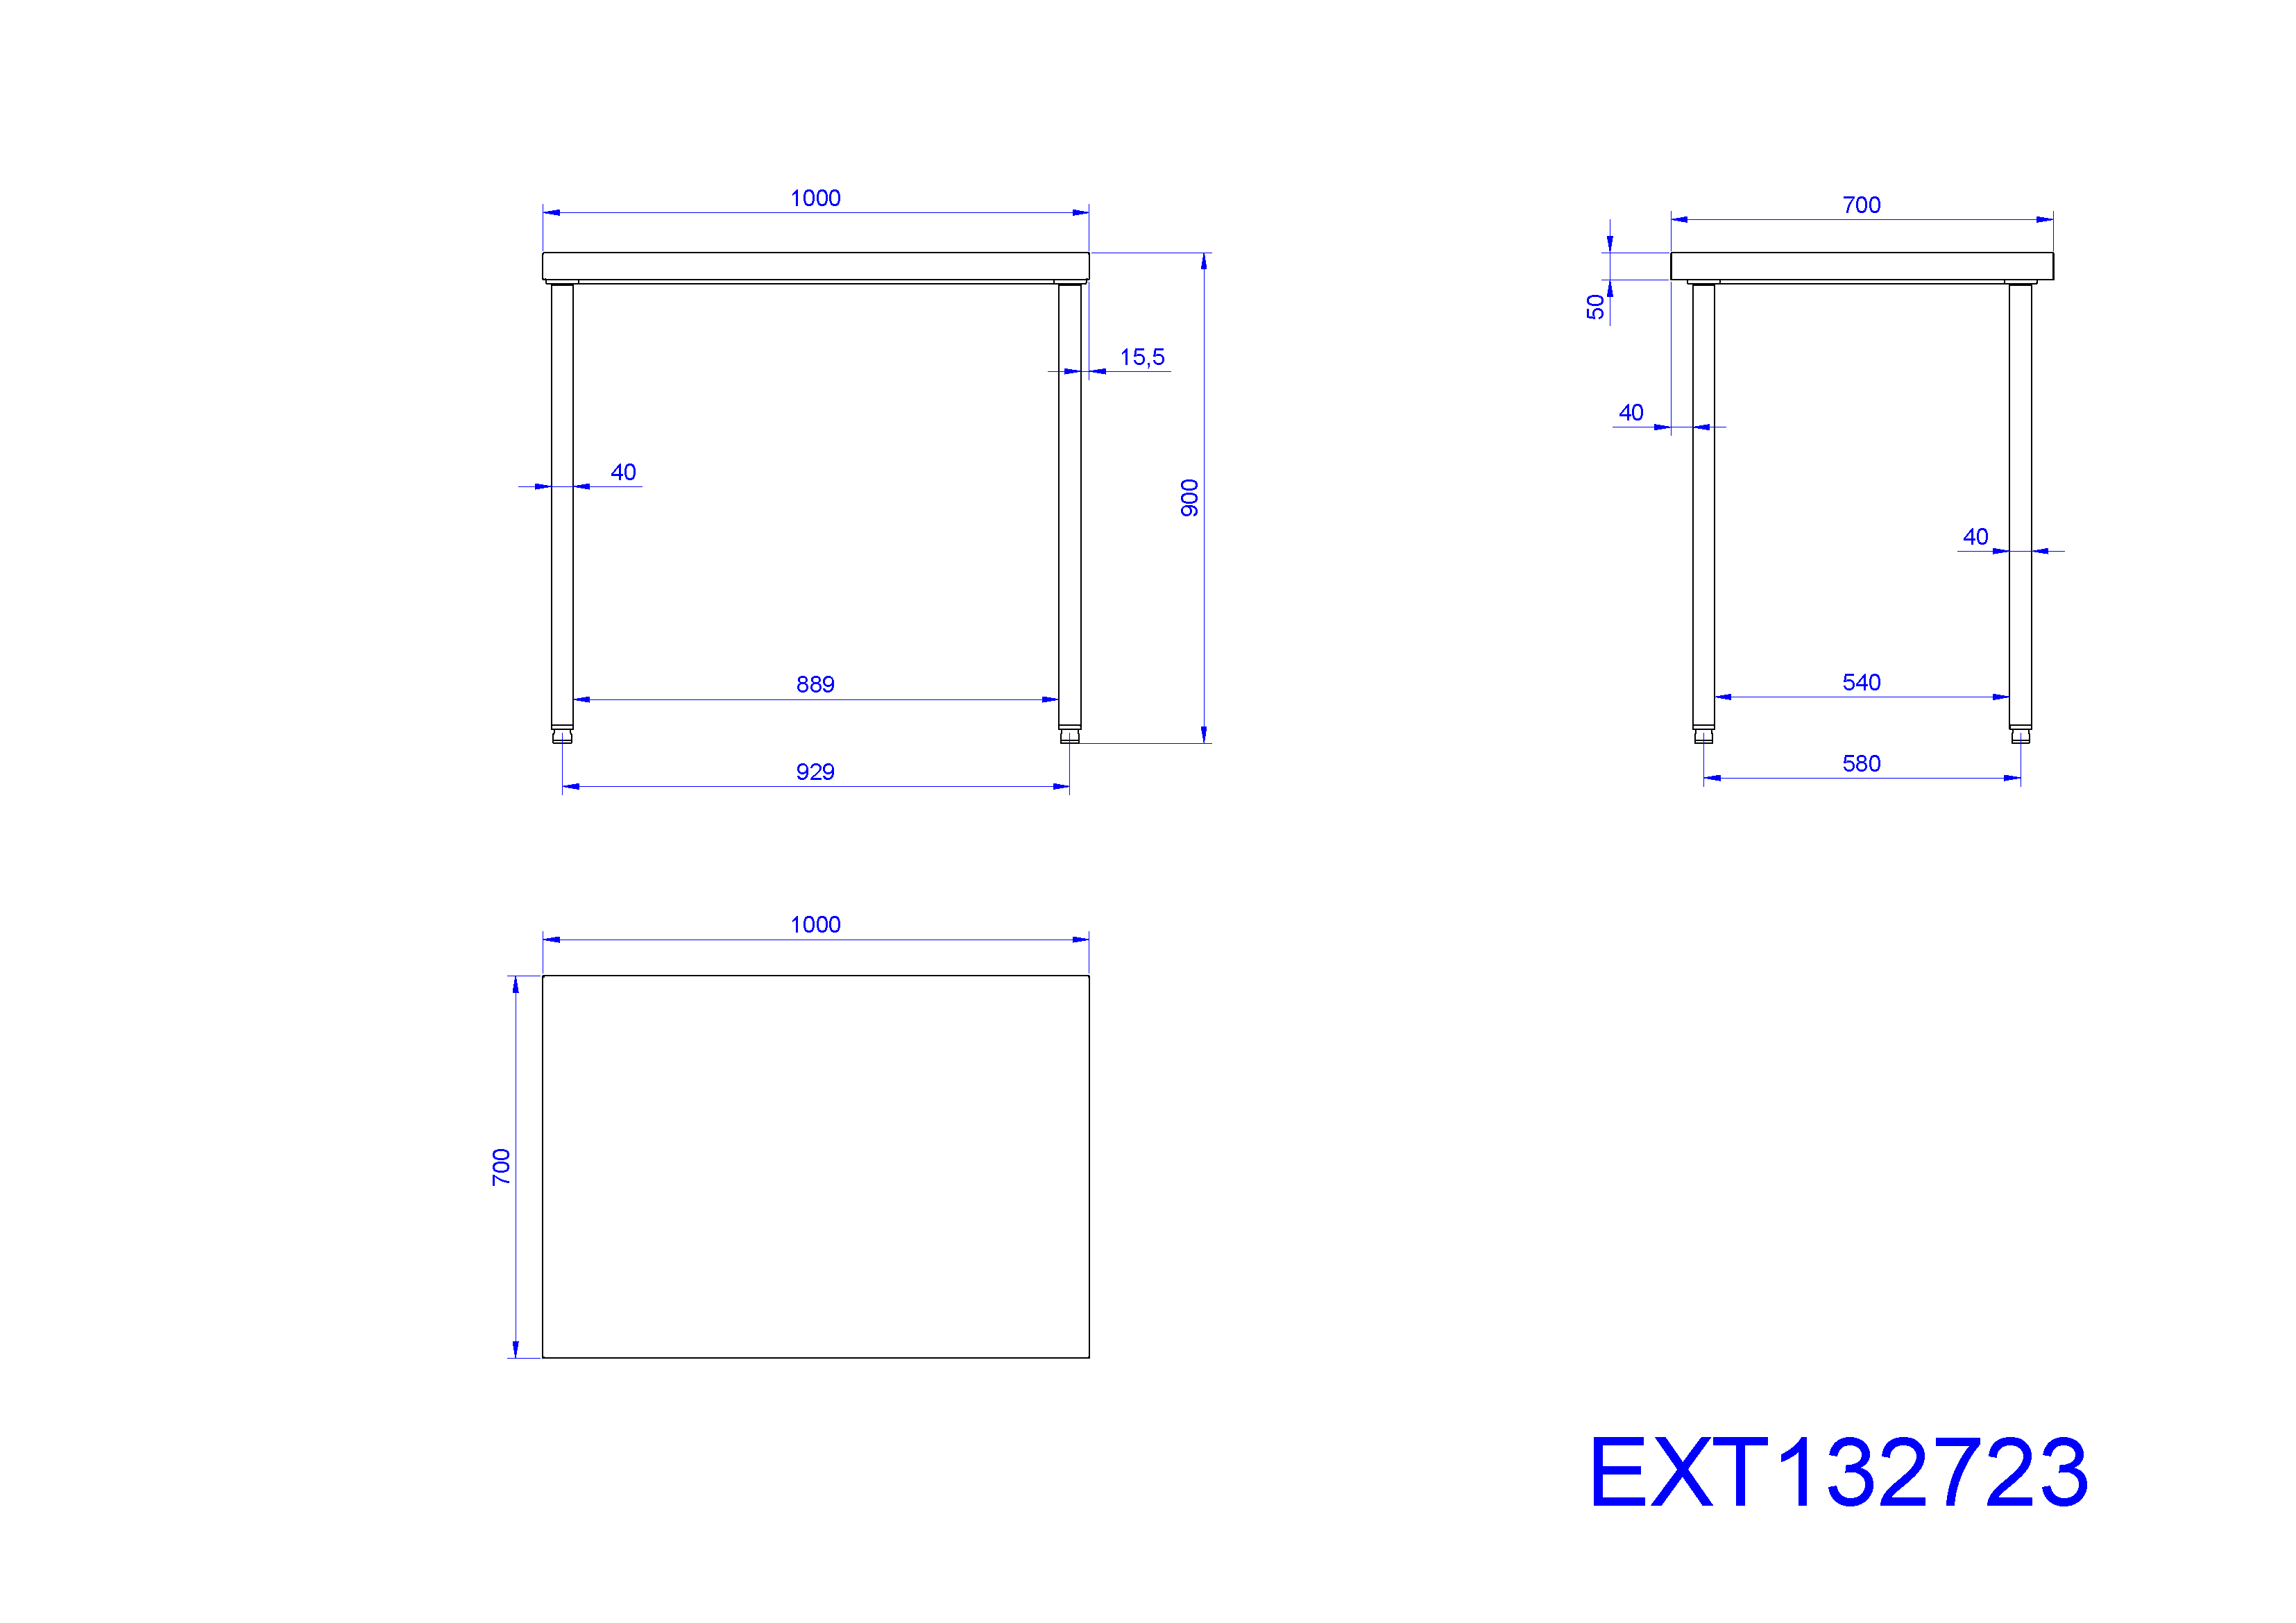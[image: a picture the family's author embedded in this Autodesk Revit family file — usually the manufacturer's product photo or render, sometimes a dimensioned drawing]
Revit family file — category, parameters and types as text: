
# Revit family: QF_ELECTROLUXPROFESSIONAL_134142_GLG2126SXP
name_source: partatom
category: Attrezzature speciali
units: mm (PartAtom-declared; Revit-internal decimal feet)

## family parameters
Basato su piano di lavoro = No
Condiviso = No
Punto di calcolo locali = No
Quota connettore circolare = Usa diametro
Sempre verticale = Sì
Taglio con vuoti quando caricato = No
Tipo di parte = Normale

## types (1)
- Standard
    Accessory = Sì
    Cold Water Size = 0 mm
    Compressed Air Pressure = 0.0 Pa
    Compressed Air Size = 0 mm
    Compressed Air Volume = 0.0 L/s
    Condensate Return Size = 0 mm
    Cycle = 0 Hz
    Depth Actual = 700 mm  [stored 2.29659 ft]
    Descrizione = SINK CUPBOARD 2 BOWLS+L/H DRAINER 2100MM
    Direct Waste Size = 0 mm
    Gas Input Pressure = 0
    Gas KW = 0
    Gas Size = 0 mm
    HP = 0 HP
    Height Actual = 1000 mm  [stored 3.28084 ft]
    Hot Water Size = 0 mm
    Item Number = 134142
    Length Actual = 2100 mm  [stored 6.88976 ft]
    Modello = GLG2126SXP
    Phase = 0
    Produttore = Electrolux Professional
    Prospetto di default = 0 mm  [stored 0 ft]
    Refrigerant Compressor Remote = Sì
    Refrigeration Liquid Line Size = 0 mm  [stored 0 ft]
    Refrigeration Suction Line Size = 0 mm  [stored 0 ft]
    Steam Consumption per Hour = 0
    Steam Supply Maximum Pressure = 0.0 Pa
    Steam Supply Minimum Pressure = 0.0 Pa
    Steam Supply Size = 0 mm
    URL = https://www.electroluxprofessional.com
    URL Manufacturer = https://www.electroluxprofessional.com
    Volts = 0 V
    Watts = 0 W
    Weight = 77.00 kg

note: source unit labels omitted for Gas Input Pressure — the stored unit's dimension contradicts the parameter name (converter mislabeling)

note: [stored X ft] marks values corroborated as IEEE doubles in the binary element streams (Revit-internal decimal feet)

## geometry (parser evidence)
native form markers: Blend x4, Sweep x5
no freeform markers — native parametric forms only
